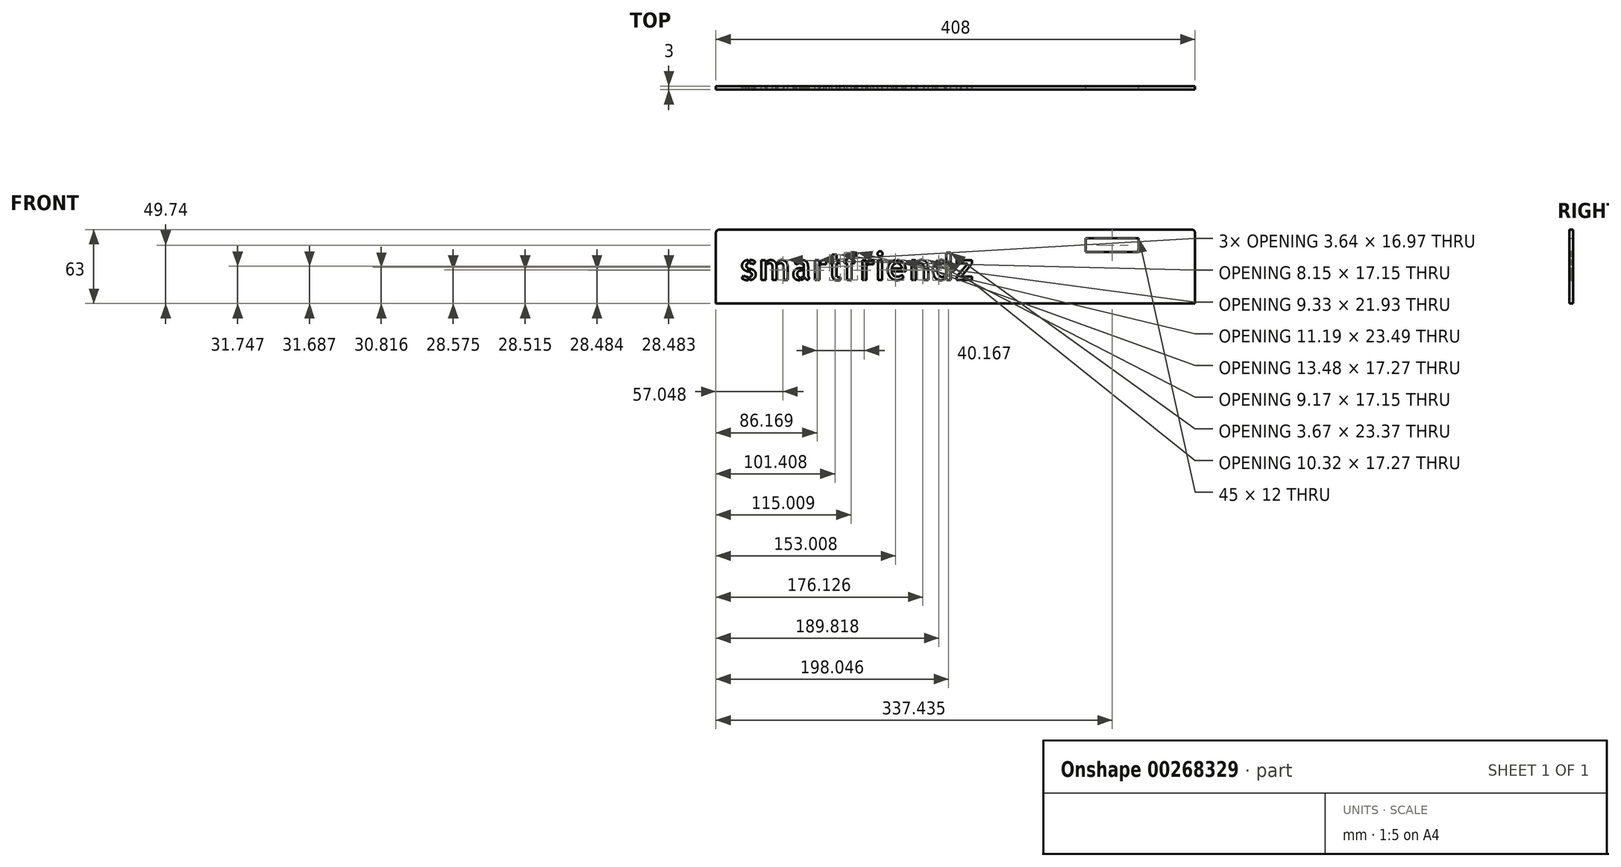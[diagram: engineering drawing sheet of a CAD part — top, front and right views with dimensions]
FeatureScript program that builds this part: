
annotation { "Feature Type Name" : "Feature", "Feature Type Description" : "" }
export const myFeature = defineFeature(function(context is Context, id is Id, definition is map)
    precondition{}
    {
        {
            var Q0;
            Q0=qCreatedBy(makeId("Front.planeOp"),FACE);
            var sketch = newSketch(context, id + "F0", { "sketchPlane" : qUnion([Q0])});
            skLineSegment(sketch, "E0.bottom", {"start": v(-241.01, -74.34) * mm, "end": v(160.99, -74.34) * mm});
            skLineSegment(sketch, "E0.top", {"start": v(-244.01, -137.34) * mm, "end": v(163.99, -137.34) * mm});
            skLineSegment(sketch, "E0.left", {"start": v(-244.01, -77.34) * mm, "end": v(-244.01, -137.34) * mm});
            skLineSegment(sketch, "E0.right", {"start": v(163.99, -77.34) * mm, "end": v(163.99, -137.34) * mm});
            skPoint(sketch, "E1.visualSharp", {"position": v(-244.01, -74.34) * mm});
            skArc(sketch, "E1.filletArc", {"start": v(-241.01, -74.34) * mm, "mid": v(-243.14, -75.22) * mm, "end": v(-244.01, -77.34) * mm});
            skPoint(sketch, "E2.visualSharp", {"position": v(163.99, -74.34) * mm});
            skArc(sketch, "E2.filletArc", {"start": v(163.99, -77.34) * mm, "mid": v(163.1, -75.22) * mm, "end": v(160.99, -74.34) * mm});
            skPoint(sketch, "E3.centerSnap0", {"position": v(163.99, -107.34) * mm});
            skText(sketch, "E4", { "text": "smartfriendz", "fontName": "AllertaStencil-Regular.ttf"});
            skLineSegment(sketch, "E5.bottom", {"start": v(70.92, -81.6) * mm, "end": v(115.92, -81.6) * mm});
            skLineSegment(sketch, "E5.top", {"start": v(70.92, -93.6) * mm, "end": v(115.92, -93.6) * mm});
            skLineSegment(sketch, "E5.left", {"start": v(70.92, -81.6) * mm, "end": v(70.92, -93.6) * mm});
            skLineSegment(sketch, "E5.right", {"start": v(115.92, -81.6) * mm, "end": v(115.92, -93.6) * mm});
            const initialGuessF0  = {"E4": [-0.22401, -0.11734, 1, 0, 0.02218]};
            skSetInitialGuess(sketch, initialGuessF0);
            skSolve(sketch);
        }
        {
            var Q0;
            Q0=qSketchRegion(id+"F0",true);
            extrude(context, id + "F1", {"entities" : qUnion([Q0]), "depth" : 3 * mm});
        }
    });
